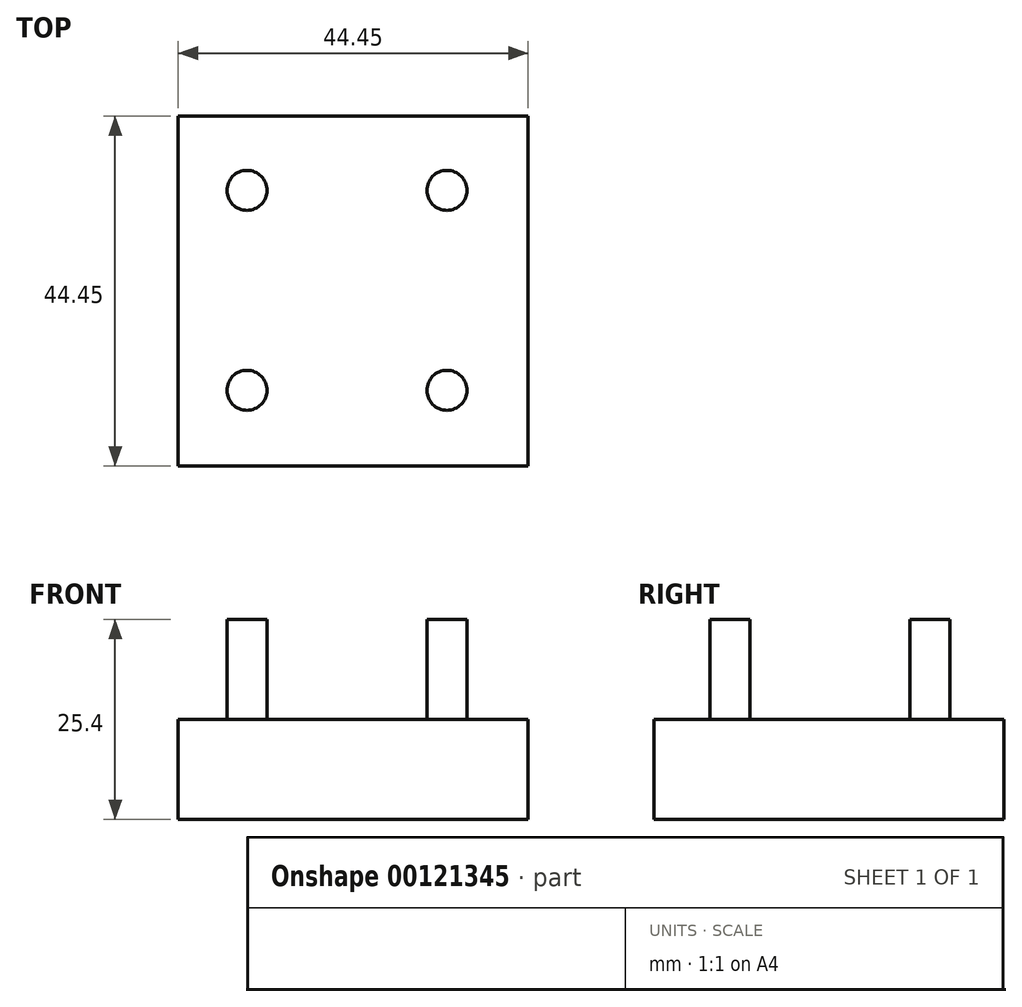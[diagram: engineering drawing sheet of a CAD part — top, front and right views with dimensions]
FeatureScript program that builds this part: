
annotation { "Feature Type Name" : "Feature", "Feature Type Description" : "" }
export const myFeature = defineFeature(function(context is Context, id is Id, definition is map)
    precondition{}
    {
        {
            var Q0;
            Q0=qCreatedBy(makeId("Top.planeOp"),FACE);
            var sketch = newSketch(context, id + "F0", { "sketchPlane" : qUnion([Q0])});
            skLineSegment(sketch, "E0.bottom", {"start": v(-22.9, -27.4) * mm, "end": v(21.55, -27.4) * mm});
            skLineSegment(sketch, "E0.top", {"start": v(-22.9, 17.06) * mm, "end": v(21.55, 17.06) * mm});
            skLineSegment(sketch, "E0.left", {"start": v(-22.9, -27.4) * mm, "end": v(-22.9, 17.06) * mm});
            skLineSegment(sketch, "E0.right", {"start": v(21.55, -27.4) * mm, "end": v(21.55, 17.06) * mm});
            skSolve(sketch);
        }
        {
            var Q0;
            Q0 = qSketchRegion(id + "F0", true);
            extrude(context, id + "F1", {"entities" : qUnion([Q0]), "depth" : 12.7 * mm});
        }
        {
            var Q0;
            Q0=makeQuery(id+"F1.opExtrude","CAP_FACE",FACE,{"disambiguationData":[OSD([sQuery(id+"F0.wireOp",EDGE,"E0.bottom"),sQuery(id+"F0.wireOp",EDGE,"E0.top"),sQuery(id+"F0.wireOp",EDGE,"E0.left"),sQuery(id+"F0.wireOp",EDGE,"E0.right")])],"isStart":false});
            var sketch = newSketch(context, id + "F2", { "sketchPlane" : qUnion([Q0])});
            skCircle(sketch, "E1", {"center": v(-14.17, 7.62) * mm, "radius": 2.54 * mm});
            skCircle(sketch, "E2.0.1.0", {"center": v(-14.17, -17.78) * mm, "radius": 2.54 * mm});
            skCircle(sketch, "E2.1.0.0", {"center": v(11.23, 7.62) * mm, "radius": 2.54 * mm});
            skCircle(sketch, "E2.1.1.0", {"center": v(11.23, -17.78) * mm, "radius": 2.54 * mm});
            skLineSegment(sketch, "E2.direction1", {"start": v(-14.17, 7.62) * mm, "end": v(11.23, 7.62) * mm, "construction": true});
            skLineSegment(sketch, "E2.direction2", {"start": v(-14.17, 7.62) * mm, "end": v(-14.17, -17.78) * mm, "construction": true});
            skSolve(sketch);
        }
        {
            var Q0;
            Q0 = qSketchRegion(id + "F2", true);
            extrude(context, id + "F3", {"entities" : qUnion([Q0]), "operationType" : NewBodyOperationType.ADD, "depth" : 12.7 * mm});
        }
    });
